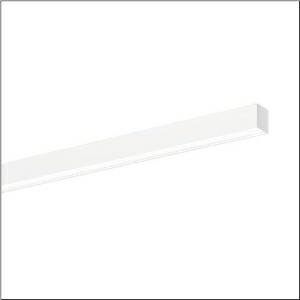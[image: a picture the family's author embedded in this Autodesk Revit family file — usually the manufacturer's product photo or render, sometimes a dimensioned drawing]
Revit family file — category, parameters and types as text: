
# Revit family: silica_21_51mx20db32wb
name_source: partatom
category: Lighting Fixtures
units: mm (PartAtom-declared; Revit-internal decimal feet)

## family parameters
Cut with Voids When Loaded = No
Host = Face
Light Source = No
Part Type = Normal
Room Calculation Point = No
Round Connector Dimension = Use Diameter
Shared = No

## types (1)
- --- (1 x LED, 3000 lm, 20.2 W, 3000K)
    Apparent Load = 20 VA
    CIE Flux Codes = 48 79 96 100 100
    Color Rendering = 80
    Color Temperature = 3000K
    Default Elevation = 1800 mm
    Description = Silica 21, office luminaire, primary optical cover: cover, of PMMA, opal, light emission: direct distribution, primary light characteristic: symmetric, installation type: surface-mounted, LED, rated luminous flux: 3.000lm, luminous efficacy: 149lm/W, light colour: 830, colour temperature: 3000K, control gear: DALI 2, with terminal, 3+2-pole, max. 2.5mm², mains connection: 220..240V, AC, 50/60Hz, luminaire housing, of aluminium, traffic white (RAL 9016), length: 1.504mm, width: 53mm, height: 53mm, protection rating (complete): IP20, insulation class (complete): insulation class I (protective earthing), certification: CE, permissible operating ambient temperature: 0..+35°C, standard: EN 50419, packaging unit: 1 piece
    Height = 53 mm
    Lamp = 1 x LED
    Lamp Light Flux = 3000 lm
    Lamp Power = 20.2 W
    Lamp count = 1
    Length = 1504 mm
    Luminous efficacy = 149 lm/W
    Manufacturer = Siteco
    ModVariant = No
    Model = 51MX20DB32WB
    Mounting Place = Ceiling
    Mounting Type = Surface mounted
    Number of Poles = 1
    OnlyDefault = Yes
    Power Factor = 1
    Product Name = Silica 21
    Product group = office luminaire | ceiling mounted
    ProductGroupID = 301
    Protection Class = Protection class I
    Protection Degree = IP 20
    RLX_Detail_Level = 1
    RLX_Emergency_Light_Flux = 0 lm
    RLX_Emergency_Type = 0
    RLX_Emergency_Type_DB = No
    RlxData = <blob elided: 23661 chars, md5=a51cb4cc>
    Socket = socket
    Standby Power = 0 W
    System Light Flux = 3000 lm
    System Power = 20 W
    Type Comments = factory setting: luminous flux: 100 % | dim-lin: 254 | 233 mA
    Type Image = l_1335877.jpg
    URL = http://relux.com
    VarID = @adj_118297
    Voltage = 0 V
    Weight = 0.00 kg
    Width = 53 mm

## geometry (parser evidence)
native form markers: Blend x4, Sweep x11
no freeform markers — native parametric forms only
